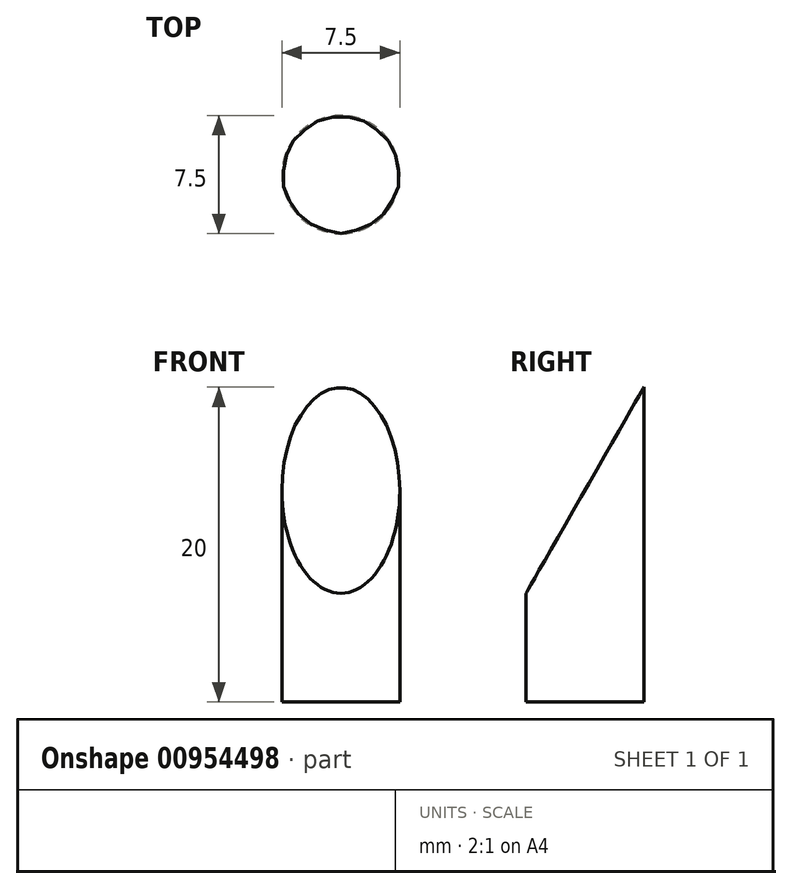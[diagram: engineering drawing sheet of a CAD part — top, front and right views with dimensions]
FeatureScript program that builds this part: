
annotation { "Feature Type Name" : "Feature", "Feature Type Description" : "" }
export const myFeature = defineFeature(function(context is Context, id is Id, definition is map)
    precondition{}
    {
        {
            var Q0;
            Q0=qCreatedBy(makeId("Top.planeOp"),FACE);
            var sketch = newSketch(context, id + "F0", { "sketchPlane" : qUnion([Q0])});
            skCircle(sketch, "E0", {"center": v(0, 0) * mm, "radius": 3.75 * mm});
            skSolve(sketch);
        }
        {
            var Q0;
            Q0 = qSketchRegion(id + "F0", true);
            extrude(context, id + "F1", {"entities" : qUnion([Q0]), "depth" : 20 * mm, "offsetDistance" : 25 * mm});
        }
        {
            var Q0;
            Q0=qCreatedBy(makeId("Right.planeOp"),FACE);
            var sketch = newSketch(context, id + "F2", { "sketchPlane" : qUnion([Q0])});
            skLineSegment(sketch, "E1", {"start": v(3.75, 20) * mm, "end": v(-3.75, 6.9) * mm});
            skLineSegment(sketch, "E2", {"start": v(-3.75, 6.9) * mm, "end": v(-16.84, 38.72) * mm});
            skLineSegment(sketch, "E3", {"start": v(-16.84, 38.72) * mm, "end": v(4.06, 47.32) * mm});
            skLineSegment(sketch, "E4", {"start": v(4.06, 47.32) * mm, "end": v(3.75, 20) * mm});
            skSolve(sketch);
        }
        {
            var Q0;
            Q0 = qSketchRegion(id + "F2", true);
            extrude(context, id + "F3", {"entities" : qUnion([Q0]), "operationType" : NewBodyOperationType.REMOVE, "oppositeDirection" : true, "depth" : 26 * mm, "offsetDistance" : 25 * mm, "hasSecondDirection" : true, "secondDirectionOppositeDirection" : false, "secondDirectionDepth" : 25 * mm});
        }
    });
